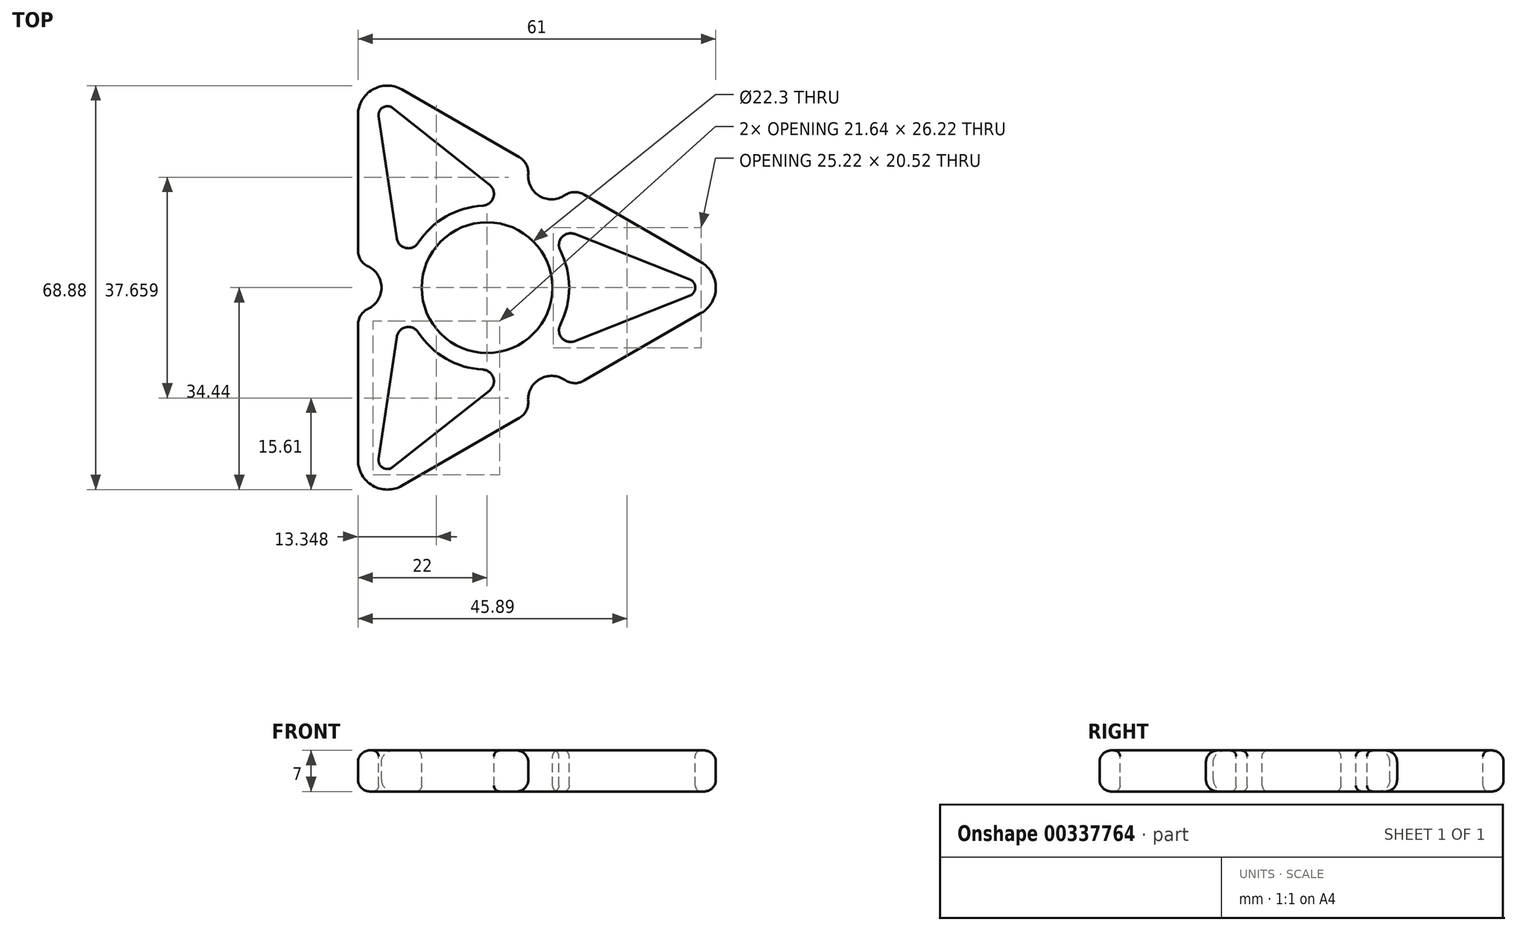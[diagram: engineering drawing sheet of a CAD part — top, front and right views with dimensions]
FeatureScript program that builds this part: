
annotation { "Feature Type Name" : "Feature", "Feature Type Description" : "" }
export const myFeature = defineFeature(function(context is Context, id is Id, definition is map)
    precondition{}
    {
        {
            var Q0;
            Q0=qCreatedBy(makeId("Top.planeOp"),FACE);
            var sketch = newSketch(context, id + "F0", { "sketchPlane" : qUnion([Q0])});
            skCircle(sketch, "E0.cCircle", {"center": v(0, 0) * mm, "radius": 22 * mm, "construction": true});
            skLineSegment(sketch, "E0.0", {"start": v(-22, -29.44) * mm, "end": v(-22, 29.44) * mm});
            skLineSegment(sketch, "E0.1", {"start": v(-14.5, 33.77) * mm, "end": v(36.5, 4.33) * mm});
            skLineSegment(sketch, "E0.2", {"start": v(36.5, -4.33) * mm, "end": v(-14.5, -33.77) * mm});
            skPoint(sketch, "E0.0.midPoint", {"position": v(-22, 0) * mm});
            skPoint(sketch, "E1.visualSharp", {"position": v(-22, 38.1) * mm});
            skArc(sketch, "E1.filletArc", {"start": v(-14.5, 33.77) * mm, "mid": v(-19.5, 33.77) * mm, "end": v(-22, 29.44) * mm});
            skPoint(sketch, "E2.visualSharp", {"position": v(44, 0) * mm});
            skArc(sketch, "E2.filletArc", {"start": v(36.5, -4.33) * mm, "mid": v(39, 0) * mm, "end": v(36.5, 4.33) * mm});
            skPoint(sketch, "E3.visualSharp", {"position": v(-22, -38.1) * mm});
            skArc(sketch, "E3.filletArc", {"start": v(-22, -29.44) * mm, "mid": v(-19.5, -33.77) * mm, "end": v(-14.5, -33.77) * mm});
            skSolve(sketch);
        }
        {
            var Q0;
            Q0=makeQuery(id+"F0.imprint","IMPRINT",FACE,{"disambiguationData":[TD([[makeQuery(id+"F0.imprint","IMPRINT",EDGE,{"derivedFrom":sQuery(id+"F0.wireOp",EDGE,"E0.0")}),-1.0]])]});
            extrude(context, id + "F1", {"entities" : qUnion([Q0]), "depth" : 7 * mm});
        }
        {
            var Q0;
            Q0=makeQuery(id+"F1.opExtrude","CAP_FACE",FACE,{"disambiguationData":[OSD([sQuery(id+"F0.wireOp",EDGE,"E0.0"),sQuery(id+"F0.wireOp",EDGE,"E0.1"),sQuery(id+"F0.wireOp",EDGE,"E0.2"),sQuery(id+"F0.wireOp",EDGE,"E1.filletArc"),sQuery(id+"F0.wireOp",EDGE,"E2.filletArc"),sQuery(id+"F0.wireOp",EDGE,"E3.filletArc")])],"isStart":false});
            var sketch = newSketch(context, id + "F2", { "sketchPlane" : qUnion([Q0])});
            skCircle(sketch, "E4", {"center": v(0, 0) * mm, "radius": 11.15 * mm});
            skSolve(sketch);
        }
        {
            var Q0;
            Q0 = qSketchRegion(id + "F2", true);
            extrude(context, id + "F3", {"entities" : qUnion([Q0]), "operationType" : NewBodyOperationType.REMOVE, "endBound" : BoundingType.THROUGH_ALL, "oppositeDirection" : true, "depth" : 25 * mm});
        }
        {
            var Q0;
            Q0=makeQuery(id+"F1.opExtrude","CAP_FACE",FACE,{"disambiguationData":[OSD([sQuery(id+"F0.wireOp",EDGE,"E0.0"),sQuery(id+"F0.wireOp",EDGE,"E0.1"),sQuery(id+"F0.wireOp",EDGE,"E0.2"),sQuery(id+"F0.wireOp",EDGE,"E1.filletArc"),sQuery(id+"F0.wireOp",EDGE,"E2.filletArc"),sQuery(id+"F0.wireOp",EDGE,"E3.filletArc")])],"isStart":false});
            var sketch = newSketch(context, id + "F4", { "sketchPlane" : qUnion([Q0])});
            skArc(sketch, "E5", {"start": v(12.47, -6.36) * mm, "mid": v(14, 0) * mm, "end": v(12.47, 6.36) * mm});
            skArc(sketch, "E6", {"start": v(34.55, -1.4) * mm, "mid": v(35.5, 0) * mm, "end": v(34.55, 1.4) * mm});
            skLineSegment(sketch, "E7", {"start": v(14.99, 9.13) * mm, "end": v(34.55, 1.4) * mm});
            skLineSegment(sketch, "E8", {"start": v(34.55, -1.4) * mm, "end": v(14.99, -9.13) * mm});
            skPoint(sketch, "E9.visualSharp", {"position": v(5.15, 13.02) * mm});
            skArc(sketch, "E9.filletArc", {"start": v(14.99, 9.13) * mm, "mid": v(12.77, 8.61) * mm, "end": v(12.47, 6.36) * mm});
            skPoint(sketch, "E10.visualSharp", {"position": v(5.15, -13.02) * mm});
            skArc(sketch, "E10.filletArc", {"start": v(12.47, -6.36) * mm, "mid": v(12.77, -8.61) * mm, "end": v(14.99, -9.13) * mm});
            skArc(sketch, "E11.1.0", {"start": v(-16.07, 30.62) * mm, "mid": v(-17.75, 30.74) * mm, "end": v(-18.48, 29.22) * mm});
            skLineSegment(sketch, "E11.1.1", {"start": v(-15.4, 8.42) * mm, "end": v(-18.48, 29.22) * mm});
            skPoint(sketch, "E11.1.2", {"position": v(8.7, 10.97) * mm});
            skPoint(sketch, "E11.1.3", {"position": v(-13.85, -2.05) * mm});
            skArc(sketch, "E11.1.4", {"start": v(-0.73, 13.98) * mm, "mid": v(1.07, 15.37) * mm, "end": v(0.41, 17.55) * mm});
            skArc(sketch, "E11.1.5", {"start": v(-0.73, 13.98) * mm, "mid": v(-7, 12.12) * mm, "end": v(-11.74, 7.62) * mm});
            skLineSegment(sketch, "E11.1.6", {"start": v(-16.07, 30.62) * mm, "end": v(0.41, 17.55) * mm});
            skArc(sketch, "E11.1.7", {"start": v(-15.4, 8.42) * mm, "mid": v(-13.85, 6.76) * mm, "end": v(-11.74, 7.62) * mm});
            skArc(sketch, "E11.2.0", {"start": v(-18.48, -29.22) * mm, "mid": v(-17.75, -30.74) * mm, "end": v(-16.07, -30.62) * mm});
            skLineSegment(sketch, "E11.2.1", {"start": v(0.41, -17.55) * mm, "end": v(-16.07, -30.62) * mm});
            skPoint(sketch, "E11.2.2", {"position": v(-13.85, 2.05) * mm});
            skPoint(sketch, "E11.2.3", {"position": v(8.7, -10.97) * mm});
            skArc(sketch, "E11.2.4", {"start": v(-11.74, -7.62) * mm, "mid": v(-13.85, -6.76) * mm, "end": v(-15.4, -8.42) * mm});
            skArc(sketch, "E11.2.5", {"start": v(-11.74, -7.62) * mm, "mid": v(-7, -12.12) * mm, "end": v(-0.73, -13.98) * mm});
            skLineSegment(sketch, "E11.2.6", {"start": v(-18.48, -29.22) * mm, "end": v(-15.4, -8.42) * mm});
            skArc(sketch, "E11.2.7", {"start": v(0.41, -17.55) * mm, "mid": v(1.07, -15.37) * mm, "end": v(-0.73, -13.98) * mm});
            skSolve(sketch);
        }
        {
            var Q0;
            Q0=makeQuery(id+"F1.opExtrude","CAP_FACE",FACE,{"disambiguationData":[OSD([sQuery(id+"F0.wireOp",EDGE,"E0.0"),sQuery(id+"F0.wireOp",EDGE,"E0.1"),sQuery(id+"F0.wireOp",EDGE,"E0.2"),sQuery(id+"F0.wireOp",EDGE,"E1.filletArc"),sQuery(id+"F0.wireOp",EDGE,"E2.filletArc"),sQuery(id+"F0.wireOp",EDGE,"E3.filletArc")])],"isStart":false});
            var sketch = newSketch(context, id + "F5", { "sketchPlane" : qUnion([Q0])});
            skArc(sketch, "E12", {"start": v(-20.29, -3.61) * mm, "mid": v(-18, 0) * mm, "end": v(-20.29, 3.61) * mm});
            skPoint(sketch, "E13.visualSharp", {"position": v(-22, 4) * mm});
            skArc(sketch, "E13.filletArc", {"start": v(-22, 6.32) * mm, "mid": v(-21.54, 4.72) * mm, "end": v(-20.29, 3.61) * mm});
            skPoint(sketch, "E14.visualSharp", {"position": v(-22, -4) * mm});
            skArc(sketch, "E14.filletArc", {"start": v(-20.29, -3.61) * mm, "mid": v(-21.54, -4.72) * mm, "end": v(-22, -6.32) * mm});
            skLineSegment(sketch, "E15", {"start": v(-22, 6.32) * mm, "end": v(-22, -6.32) * mm});
            skArc(sketch, "E16.1.0", {"start": v(13.27, -15.76) * mm, "mid": v(9, -15.59) * mm, "end": v(7.01, -19.37) * mm});
            skPoint(sketch, "E16.1.1", {"position": v(14.46, -17.05) * mm});
            skLineSegment(sketch, "E16.1.2", {"start": v(5.52, -22.21) * mm, "end": v(16.48, -15.9) * mm});
            skPoint(sketch, "E16.1.3", {"position": v(7.54, -21.05) * mm});
            skArc(sketch, "E16.1.4", {"start": v(5.52, -22.21) * mm, "mid": v(6.68, -21.01) * mm, "end": v(7.01, -19.37) * mm});
            skArc(sketch, "E16.1.5", {"start": v(13.27, -15.76) * mm, "mid": v(14.86, -16.29) * mm, "end": v(16.48, -15.9) * mm});
            skArc(sketch, "E16.2.0", {"start": v(7.01, 19.37) * mm, "mid": v(9, 15.59) * mm, "end": v(13.27, 15.76) * mm});
            skPoint(sketch, "E16.2.1", {"position": v(7.54, 21.05) * mm});
            skLineSegment(sketch, "E16.2.2", {"start": v(16.48, 15.9) * mm, "end": v(5.52, 22.21) * mm});
            skPoint(sketch, "E16.2.3", {"position": v(14.46, 17.05) * mm});
            skArc(sketch, "E16.2.4", {"start": v(16.48, 15.9) * mm, "mid": v(14.86, 16.29) * mm, "end": v(13.27, 15.76) * mm});
            skArc(sketch, "E16.2.5", {"start": v(7.01, 19.37) * mm, "mid": v(6.68, 21.01) * mm, "end": v(5.52, 22.21) * mm});
            skPoint(sketch, "E16.center", {"position": v(0, 0) * mm});
            skSolve(sketch);
        }
        {
            var Q0;
            Q0 = qSketchRegion(id + "F5", true);
            extrude(context, id + "F6", {"entities" : qUnion([Q0]), "operationType" : NewBodyOperationType.REMOVE, "endBound" : BoundingType.THROUGH_ALL, "oppositeDirection" : true, "depth" : 25 * mm});
        }
        {
            var Q0;
            {var subQ0=sQuery(id+"F0.wireOp",EDGE,"E3.filletArc");var subQ3=sQuery(id+"F0.wireOp",EDGE,"E0.2");Q0=makeQuery(id+"F6.boolean.opBoolean","SPLIT",FACE,{"disambiguationData":[TD([makeQuery(id+"F1.opExtrude","SWEPT_FACE",FACE,{"disambiguationData":[OSD([subQ0])]})])],"derivedFrom":makeQuery(id+"F1.opExtrude","SWEPT_FACE",FACE,{"disambiguationData":[OSD([subQ3])]})});}
            var Q1;
            Q1=makeQuery(id+"F6.boolean.opBoolean","COPY",FACE,{"derivedFrom":makeQuery(id+"F6.opExtrude","SWEPT_FACE",FACE,{"disambiguationData":[OSD([sQuery(id+"F5.wireOp",EDGE,"E16.1.4")])]})});
            var Q2;
            Q2=makeQuery(id+"F6.boolean.opBoolean","COPY",FACE,{"derivedFrom":makeQuery(id+"F6.opExtrude","SWEPT_FACE",FACE,{"disambiguationData":[OSD([sQuery(id+"F5.wireOp",EDGE,"E16.1.0")])]})});
            var Q3;
            Q3=makeQuery(id+"F6.boolean.opBoolean","COPY",FACE,{"derivedFrom":makeQuery(id+"F6.opExtrude","SWEPT_FACE",FACE,{"disambiguationData":[OSD([sQuery(id+"F5.wireOp",EDGE,"E16.1.5")])]})});
            var Q4;
            {var subQ1=sQuery(id+"F0.wireOp",EDGE,"E2.filletArc");var subQ3=sQuery(id+"F0.wireOp",EDGE,"E0.2");Q4=makeQuery(id+"F6.boolean.opBoolean","SPLIT",FACE,{"disambiguationData":[TD([makeQuery(id+"F1.opExtrude","SWEPT_FACE",FACE,{"disambiguationData":[OSD([subQ1])]})])],"derivedFrom":makeQuery(id+"F1.opExtrude","SWEPT_FACE",FACE,{"disambiguationData":[OSD([subQ3])]})});}
            var Q5;
            Q5=makeQuery(id+"F1.opExtrude","SWEPT_FACE",FACE,{"disambiguationData":[OSD([sQuery(id+"F0.wireOp",EDGE,"E2.filletArc")])]});
            var Q6;
            Q6=makeQuery(id+"F1.opExtrude","SWEPT_FACE",FACE,{"disambiguationData":[OSD([sQuery(id+"F0.wireOp",EDGE,"E3.filletArc")])]});
            var Q7;
            {var subQ0=sQuery(id+"F0.wireOp",EDGE,"E3.filletArc");var subQ5=sQuery(id+"F0.wireOp",EDGE,"E0.0");Q7=makeQuery(id+"F6.boolean.opBoolean","SPLIT",FACE,{"disambiguationData":[TD([makeQuery(id+"F1.opExtrude","SWEPT_FACE",FACE,{"disambiguationData":[OSD([subQ0])]})])],"derivedFrom":makeQuery(id+"F1.opExtrude","SWEPT_FACE",FACE,{"disambiguationData":[OSD([subQ5])]})});}
            var Q8;
            Q8=makeQuery(id+"F6.boolean.opBoolean","COPY",FACE,{"derivedFrom":makeQuery(id+"F6.opExtrude","SWEPT_FACE",FACE,{"disambiguationData":[OSD([sQuery(id+"F5.wireOp",EDGE,"E14.filletArc")])]})});
            var Q9;
            Q9=makeQuery(id+"F6.boolean.opBoolean","COPY",FACE,{"derivedFrom":makeQuery(id+"F6.opExtrude","SWEPT_FACE",FACE,{"disambiguationData":[OSD([sQuery(id+"F5.wireOp",EDGE,"E12")])]})});
            var Q10;
            Q10=makeQuery(id+"F6.boolean.opBoolean","COPY",FACE,{"derivedFrom":makeQuery(id+"F6.opExtrude","SWEPT_FACE",FACE,{"disambiguationData":[OSD([sQuery(id+"F5.wireOp",EDGE,"E13.filletArc")])]})});
            var Q11;
            {var subQ2=sQuery(id+"F0.wireOp",EDGE,"E1.filletArc");var subQ5=sQuery(id+"F0.wireOp",EDGE,"E0.0");Q11=makeQuery(id+"F6.boolean.opBoolean","SPLIT",FACE,{"disambiguationData":[TD([makeQuery(id+"F1.opExtrude","SWEPT_FACE",FACE,{"disambiguationData":[OSD([subQ2])]})])],"derivedFrom":makeQuery(id+"F1.opExtrude","SWEPT_FACE",FACE,{"disambiguationData":[OSD([subQ5])]})});}
            var Q12;
            Q12=makeQuery(id+"F1.opExtrude","SWEPT_FACE",FACE,{"disambiguationData":[OSD([sQuery(id+"F0.wireOp",EDGE,"E1.filletArc")])]});
            var Q13;
            {var subQ2=sQuery(id+"F0.wireOp",EDGE,"E1.filletArc");var subQ4=sQuery(id+"F0.wireOp",EDGE,"E0.1");Q13=makeQuery(id+"F6.boolean.opBoolean","SPLIT",FACE,{"disambiguationData":[TD([makeQuery(id+"F1.opExtrude","SWEPT_FACE",FACE,{"disambiguationData":[OSD([subQ2])]})])],"derivedFrom":makeQuery(id+"F1.opExtrude","SWEPT_FACE",FACE,{"disambiguationData":[OSD([subQ4])]})});}
            var Q14;
            Q14=makeQuery(id+"F6.boolean.opBoolean","COPY",FACE,{"derivedFrom":makeQuery(id+"F6.opExtrude","SWEPT_FACE",FACE,{"disambiguationData":[OSD([sQuery(id+"F5.wireOp",EDGE,"E16.2.0")])]})});
            var Q15;
            Q15=makeQuery(id+"F6.boolean.opBoolean","COPY",FACE,{"derivedFrom":makeQuery(id+"F6.opExtrude","SWEPT_FACE",FACE,{"disambiguationData":[OSD([sQuery(id+"F5.wireOp",EDGE,"E16.2.4")])]})});
            var Q16;
            {var subQ1=sQuery(id+"F0.wireOp",EDGE,"E2.filletArc");var subQ4=sQuery(id+"F0.wireOp",EDGE,"E0.1");Q16=makeQuery(id+"F6.boolean.opBoolean","SPLIT",FACE,{"disambiguationData":[TD([makeQuery(id+"F1.opExtrude","SWEPT_FACE",FACE,{"disambiguationData":[OSD([subQ1])]})])],"derivedFrom":makeQuery(id+"F1.opExtrude","SWEPT_FACE",FACE,{"disambiguationData":[OSD([subQ4])]})});}
            var Q17;
            Q17=makeQuery(id+"F6.boolean.opBoolean","COPY",FACE,{"derivedFrom":makeQuery(id+"F6.opExtrude","SWEPT_FACE",FACE,{"disambiguationData":[OSD([sQuery(id+"F5.wireOp",EDGE,"E16.2.5")])]})});
            fillet(context, id + "F7", {"entities" : qUnion([Q0, Q1, Q2, Q3, Q4, Q5, Q6, Q7, Q8, Q9, Q10, Q11, Q12, Q13, Q14, Q15, Q16, Q17]), "radius" : 2 * mm, "tangentPropagation" : true, "allowEdgeOverflow" : false});
        }
        {
            var Q0;
            Q0=makeQuery(id+"F3.boolean.opBoolean","COPY",FACE,{"derivedFrom":makeQuery(id+"F3.opExtrude","SWEPT_FACE",FACE,{"disambiguationData":[OSD([sQuery(id+"F2.wireOp",EDGE,"E4")])]})});
            fillet(context, id + "F8", {"entities" : qUnion([Q0]), "radius" : 1 * mm, "tangentPropagation" : true, "allowEdgeOverflow" : false});
        }
        {
            var Q0;
            Q0 = qSketchRegion(id + "F4", true);
            extrude(context, id + "F9", {"entities" : qUnion([Q0]), "operationType" : NewBodyOperationType.REMOVE, "endBound" : BoundingType.THROUGH_ALL, "oppositeDirection" : true, "depth" : 25 * mm});
        }
        {
            var Q0;
            Q0=makeQuery(id+"F9.boolean.opBoolean","COPY",FACE,{"derivedFrom":makeQuery(id+"F9.opExtrude","SWEPT_FACE",FACE,{"disambiguationData":[OSD([sQuery(id+"F4.wireOp",EDGE,"E11.1.0")])]})});
            var Q1;
            Q1=makeQuery(id+"F9.boolean.opBoolean","COPY",FACE,{"derivedFrom":makeQuery(id+"F9.opExtrude","SWEPT_FACE",FACE,{"disambiguationData":[OSD([sQuery(id+"F4.wireOp",EDGE,"E11.1.6")])]})});
            var Q2;
            Q2=makeQuery(id+"F9.boolean.opBoolean","COPY",FACE,{"derivedFrom":makeQuery(id+"F9.opExtrude","SWEPT_FACE",FACE,{"disambiguationData":[OSD([sQuery(id+"F4.wireOp",EDGE,"E11.1.1")])]})});
            var Q3;
            Q3=makeQuery(id+"F9.boolean.opBoolean","COPY",FACE,{"derivedFrom":makeQuery(id+"F9.opExtrude","SWEPT_FACE",FACE,{"disambiguationData":[OSD([sQuery(id+"F4.wireOp",EDGE,"E11.1.7")])]})});
            var Q4;
            Q4=makeQuery(id+"F9.boolean.opBoolean","COPY",FACE,{"derivedFrom":makeQuery(id+"F9.opExtrude","SWEPT_FACE",FACE,{"disambiguationData":[OSD([sQuery(id+"F4.wireOp",EDGE,"E11.1.5")])]})});
            var Q5;
            Q5=makeQuery(id+"F9.boolean.opBoolean","COPY",FACE,{"derivedFrom":makeQuery(id+"F9.opExtrude","SWEPT_FACE",FACE,{"disambiguationData":[OSD([sQuery(id+"F4.wireOp",EDGE,"E11.1.4")])]})});
            fillet(context, id + "F10", {"entities" : qUnion([Q0, Q1, Q2, Q3, Q4, Q5]), "radius" : 1 * mm, "tangentPropagation" : true, "allowEdgeOverflow" : false});
        }
        {
            var Q0;
            Q0=makeQuery(id+"F9.boolean.opBoolean","COPY",FACE,{"derivedFrom":makeQuery(id+"F9.opExtrude","SWEPT_FACE",FACE,{"disambiguationData":[OSD([sQuery(id+"F4.wireOp",EDGE,"E11.2.0")])]})});
            var Q1;
            Q1=makeQuery(id+"F9.boolean.opBoolean","COPY",FACE,{"derivedFrom":makeQuery(id+"F9.opExtrude","SWEPT_FACE",FACE,{"disambiguationData":[OSD([sQuery(id+"F4.wireOp",EDGE,"E11.2.1")])]})});
            var Q2;
            Q2=makeQuery(id+"F9.boolean.opBoolean","COPY",FACE,{"derivedFrom":makeQuery(id+"F9.opExtrude","SWEPT_FACE",FACE,{"disambiguationData":[OSD([sQuery(id+"F4.wireOp",EDGE,"E11.2.6")])]})});
            var Q3;
            Q3=makeQuery(id+"F9.boolean.opBoolean","COPY",FACE,{"derivedFrom":makeQuery(id+"F9.opExtrude","SWEPT_FACE",FACE,{"disambiguationData":[OSD([sQuery(id+"F4.wireOp",EDGE,"E11.2.4")])]})});
            var Q4;
            Q4=makeQuery(id+"F9.boolean.opBoolean","COPY",FACE,{"derivedFrom":makeQuery(id+"F9.opExtrude","SWEPT_FACE",FACE,{"disambiguationData":[OSD([sQuery(id+"F4.wireOp",EDGE,"E10.filletArc")])]})});
            var Q5;
            Q5=makeQuery(id+"F9.boolean.opBoolean","COPY",FACE,{"derivedFrom":makeQuery(id+"F9.opExtrude","SWEPT_FACE",FACE,{"disambiguationData":[OSD([sQuery(id+"F4.wireOp",EDGE,"E5")])]})});
            var Q6;
            Q6=makeQuery(id+"F9.boolean.opBoolean","COPY",FACE,{"derivedFrom":makeQuery(id+"F9.opExtrude","SWEPT_FACE",FACE,{"disambiguationData":[OSD([sQuery(id+"F4.wireOp",EDGE,"E9.filletArc")])]})});
            var Q7;
            Q7=makeQuery(id+"F9.boolean.opBoolean","COPY",FACE,{"derivedFrom":makeQuery(id+"F9.opExtrude","SWEPT_FACE",FACE,{"disambiguationData":[OSD([sQuery(id+"F4.wireOp",EDGE,"E11.2.7")])]})});
            var Q8;
            Q8=makeQuery(id+"F9.boolean.opBoolean","COPY",FACE,{"derivedFrom":makeQuery(id+"F9.opExtrude","SWEPT_FACE",FACE,{"disambiguationData":[OSD([sQuery(id+"F4.wireOp",EDGE,"E11.2.5")])]})});
            var Q9;
            Q9=makeQuery(id+"F9.boolean.opBoolean","COPY",FACE,{"derivedFrom":makeQuery(id+"F9.opExtrude","SWEPT_FACE",FACE,{"disambiguationData":[OSD([sQuery(id+"F4.wireOp",EDGE,"E7")])]})});
            var Q10;
            Q10=makeQuery(id+"F9.boolean.opBoolean","COPY",FACE,{"derivedFrom":makeQuery(id+"F9.opExtrude","SWEPT_FACE",FACE,{"disambiguationData":[OSD([sQuery(id+"F4.wireOp",EDGE,"E6")])]})});
            var Q11;
            Q11=makeQuery(id+"F9.boolean.opBoolean","COPY",FACE,{"derivedFrom":makeQuery(id+"F9.opExtrude","SWEPT_FACE",FACE,{"disambiguationData":[OSD([sQuery(id+"F4.wireOp",EDGE,"E8")])]})});
            fillet(context, id + "F11", {"entities" : qUnion([Q0, Q1, Q2, Q3, Q4, Q5, Q6, Q7, Q8, Q9, Q10, Q11]), "radius" : 1 * mm, "tangentPropagation" : true, "allowEdgeOverflow" : false});
        }
    });
